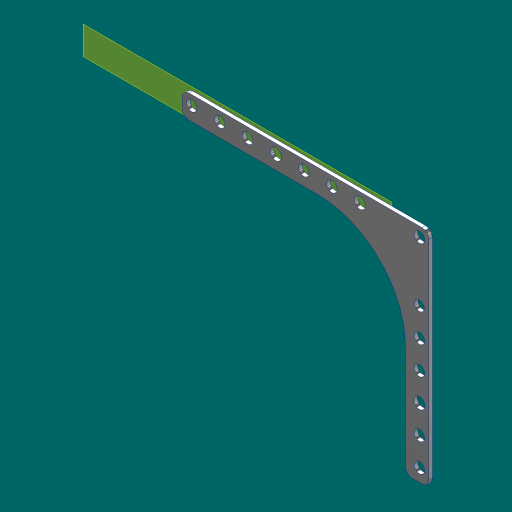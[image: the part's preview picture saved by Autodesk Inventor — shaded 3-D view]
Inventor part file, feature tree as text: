
AUTODESK INVENTOR PART (.ipt)
format: ipt  version: 2023.1 (Build 271208000, 208)  size: 148,992 bytes
history: native  units: in
note: dims shown in document units (in); Inventor stores cm internally (conversion verified against a paired STEP export)
features: reference x4, other x4, plane x1, extrude x1, fillet x1, sketch x1
ambient origin geometry x8: Origin, YZ Plane, XZ Plane, XY Plane, X Axis, Y Axis, Z Axis, Center Point
bodies: Solid1 (feature_tree)
feature tree (12):
  plane  "Work Plane1"
  extrude  "Extrusion1"  Depth=0.125in
  fillet  "Fillet1"  Radius=0.3937in
  sketch  "Sketch1"  dims[d0=0.42in d2=0.177in d3=2.3622in d5=0.5in d6=0.3937in d8=1.0in d10=0.177in d11=2.7559in d13=0.5in d14=0.3937in d16=1.0in d18=0.0625in d19=0.0in d20=0.125in]
  reference  "Reference1"
  reference  "Reference2"
  reference  "Reference3"
  reference  "Reference4"
  other  "<userpath>\Documents\CAD\guardSwerve5\MainAssy.iam"
  other  "MainAssy.iam"
  other  "Baseplate:1"
  other  "Alu C 1x2x1x10:1"
